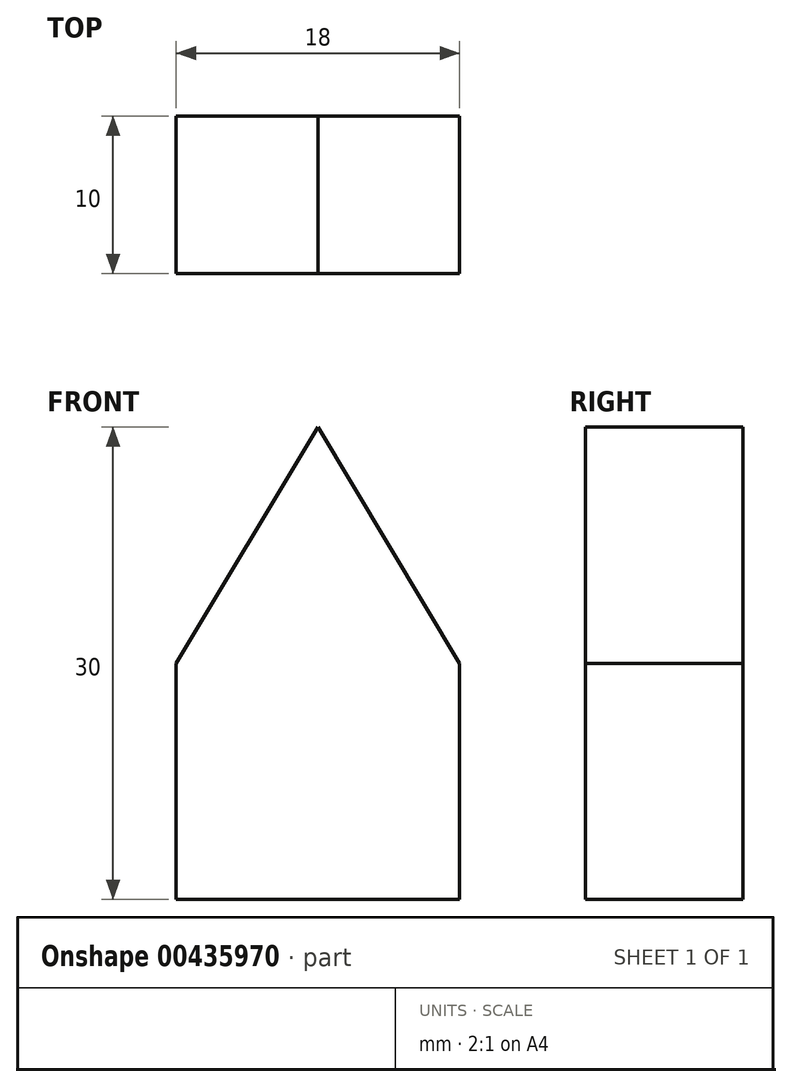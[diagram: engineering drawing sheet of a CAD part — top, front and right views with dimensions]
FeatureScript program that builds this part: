
annotation { "Feature Type Name" : "Feature", "Feature Type Description" : "" }
export const myFeature = defineFeature(function(context is Context, id is Id, definition is map)
    precondition{}
    {
        {
            var Q0;
            Q0=qCreatedBy(makeId("Front.planeOp"),FACE);
            var sketch = newSketch(context, id + "F0", { "sketchPlane" : qUnion([Q0])});
            skLineSegment(sketch, "E0.bottom", {"start": v(9, -7.5) * mm, "end": v(-9, -7.5) * mm});
            skLineSegment(sketch, "E0.top", {"start": v(9, 7.5) * mm, "end": v(-9, 7.5) * mm});
            skLineSegment(sketch, "E0.left", {"start": v(9, -7.5) * mm, "end": v(9, 7.5) * mm});
            skLineSegment(sketch, "E0.right", {"start": v(-9, -7.5) * mm, "end": v(-9, 7.5) * mm});
            skPoint(sketch, "E0.middle", {"position": v(0, 0) * mm});
            skLineSegment(sketch, "E1", {"start": v(-9, 7.5) * mm, "end": v(0, 22.5) * mm});
            skLineSegment(sketch, "E2", {"start": v(0, 22.5) * mm, "end": v(9, 7.5) * mm});
            skSolve(sketch);
        }
        {
            var Q0;
            Q0 = qSketchRegion(id + "F0", true);
            extrude(context, id + "F1", {"entities" : qUnion([Q0]), "depth" : 10 * mm});
        }
    });
